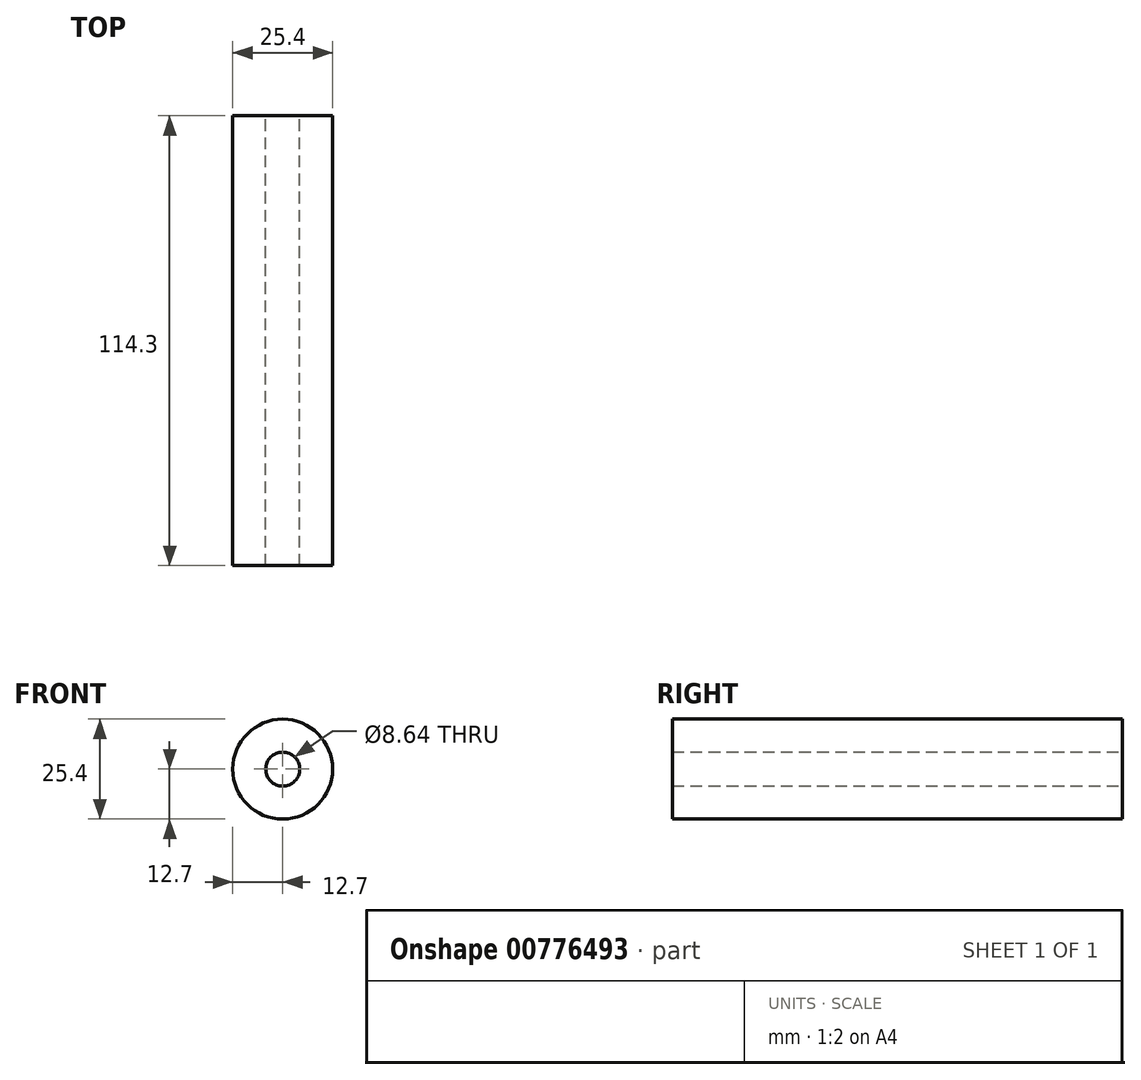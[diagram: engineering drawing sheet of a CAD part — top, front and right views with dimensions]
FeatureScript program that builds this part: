
annotation { "Feature Type Name" : "Feature", "Feature Type Description" : "" }
export const myFeature = defineFeature(function(context is Context, id is Id, definition is map)
    precondition{}
    {
        {
            var Q0;
            Q0=qCreatedBy(makeId("Front.planeOp"),FACE);
            var sketch = newSketch(context, id + "F0", { "sketchPlane" : qUnion([Q0])});
            skCircle(sketch, "E0", {"center": v(0, 0) * mm, "radius": 4.32 * mm});
            skCircle(sketch, "E1", {"center": v(0, 0) * mm, "radius": 12.7 * mm});
            skSolve(sketch);
        }
        {
            var Q0;
            Q0=qSketchRegion(id+"F0",true);
            extrude(context, id + "F1", {"entities" : qUnion([Q0]), "depth" : 114.3 * mm, "offsetDistance" : 25.4 * mm});
        }
    });
